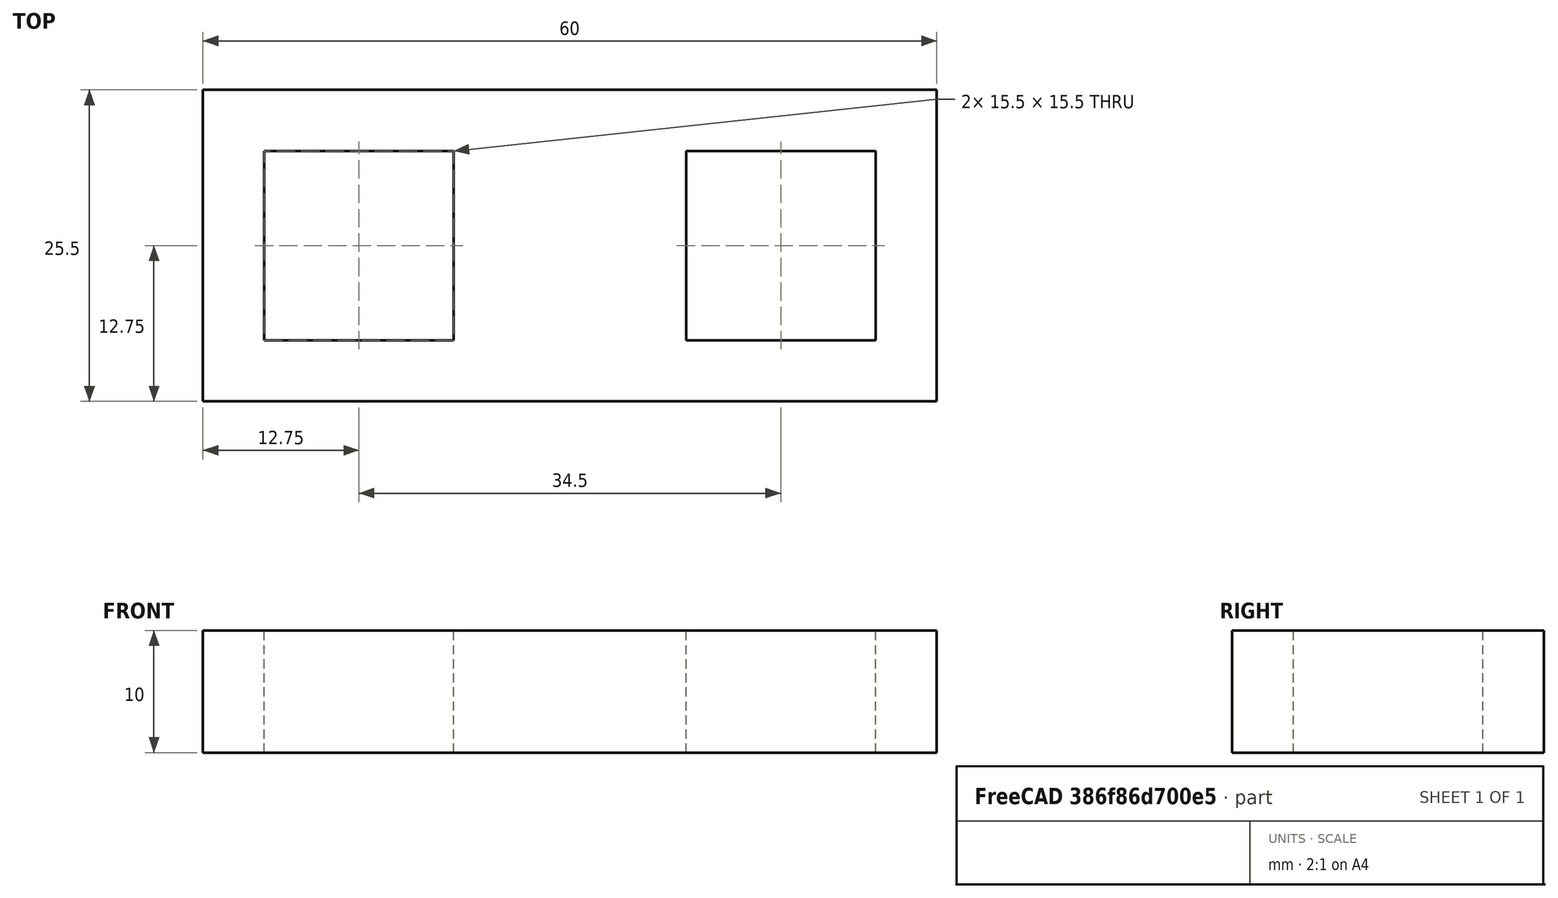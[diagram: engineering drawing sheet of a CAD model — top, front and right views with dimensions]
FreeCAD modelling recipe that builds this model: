
FCSTD DOCUMENT  (FreeCAD 0.21R33694 (Git))
Label: LcdFrame
License: All rights reserved
LicenseURL: https://en.wikipedia.org/wiki/All_rights_reserved
objects: Sketcher::SketchObject×1, PartDesign::Pad×1, PartDesign::Body×1
note: 4 computed .brp shape members not serialized (recipe doc carries the construction recipe); baked Part::Feature solids carry a one-line shape summary decoded from their .brp

FEATURE [Sketcher::SketchObject] Sketch
  FullyConstrained = true
  MapMode = 5
  Support = -> [XY_Plane]
  sketch-geometry (15):
    g0: LineSegment StartX=9.5 StartY=20.75 StartZ=0 EndX=25 EndY=20.75 EndZ=0
    g1: LineSegment StartX=25 StartY=20.75 StartZ=0 EndX=25 EndY=5.25 EndZ=0
    g2: LineSegment StartX=25 StartY=5.25 StartZ=0 EndX=9.5 EndY=5.25 EndZ=0
    g3: LineSegment StartX=9.5 StartY=5.25 StartZ=0 EndX=9.5 EndY=20.75 EndZ=0
    g4: LineSegment StartX=-25 StartY=20.75 StartZ=0 EndX=-9.5 EndY=20.75 EndZ=0
    g5: LineSegment StartX=-9.5 StartY=20.75 StartZ=0 EndX=-9.5 EndY=5.25 EndZ=0
    g6: LineSegment StartX=-9.5 StartY=5.25 StartZ=0 EndX=-25 EndY=5.25 EndZ=0
    g7: LineSegment StartX=-25 StartY=5.25 StartZ=0 EndX=-25 EndY=20.75 EndZ=0
    g8: GeomPoint X=-25 Y=13 Z=0
    g9: LineSegment StartX=-25 StartY=13 StartZ=0 EndX=25 EndY=13 EndZ=0
    g10: GeomPoint X=25 Y=13 Z=0
    g11: LineSegment StartX=-30 StartY=25.75 StartZ=0 EndX=30 EndY=25.75 EndZ=0
    g12: LineSegment StartX=30 StartY=25.75 StartZ=0 EndX=30 EndY=0.25 EndZ=0
    g13: LineSegment StartX=30 StartY=0.25 StartZ=0 EndX=-30 EndY=0.25 EndZ=0
    g14: LineSegment StartX=-30 StartY=0.25 StartZ=0 EndX=-30 EndY=25.75 EndZ=0
  constraints (39):
    c: Coincident(g0,g1)
    c: Coincident(g1,g2)
    c: Coincident(g2,g3)
    c: Coincident(g3,g0)
    c: Horizontal(g0)
    c: Horizontal(g2)
    c: Vertical(g1)
    c: Vertical(g3)
    c: Coincident(g4,g5)
    c: Coincident(g5,g6)
    c: Coincident(g6,g7)
    c: Coincident(g7,g4)
    c: Horizontal(g4)
    c: Horizontal(g6)
    c: Vertical(g5)
    c: Vertical(g7)
    c: Equal(g5,g4)
    c: Equal(g3,g0)
    c: Equal(g4,g0)
    c: DistanceX(g4,g4) = 15.5
    c: Symmetric(g6,g4,g8)
    c: Symmetric(g1,g0,g10)
    c: Coincident(g9,g8)
    c: Coincident(g10,g9)
    c: Symmetric(g8,g9,g-2)
    c: DistanceX(g8,g9) = 50
    c: Coincident(g11,g12)
    c: Coincident(g12,g13)
    c: Coincident(g13,g14)
    c: Coincident(g14,g11)
    c: Horizontal(g11)
    c: Horizontal(g13)
    c: Vertical(g12)
    c: Vertical(g14)
    c: DistanceY(g0,g11) = 5
    c: DistanceY(g12,g1) = 5
    c: DistanceX(g0,g11) = 5
    c: DistanceX(g11,g4) = 5
    c: DistanceY(g-1,g8) = 13
FEATURE [PartDesign::Pad] Pad
  Direction = (0,0,1)
  Length = 10
  Length2 = 10
  Profile = -> Sketch
  ReferenceAxis = -> Sketch [N_Axis]
  Type = 0
FEATURE [PartDesign::Body] Body
  Group = -> [Sketch,Pad]
  Origin = -> Origin
  Tip = -> Pad
